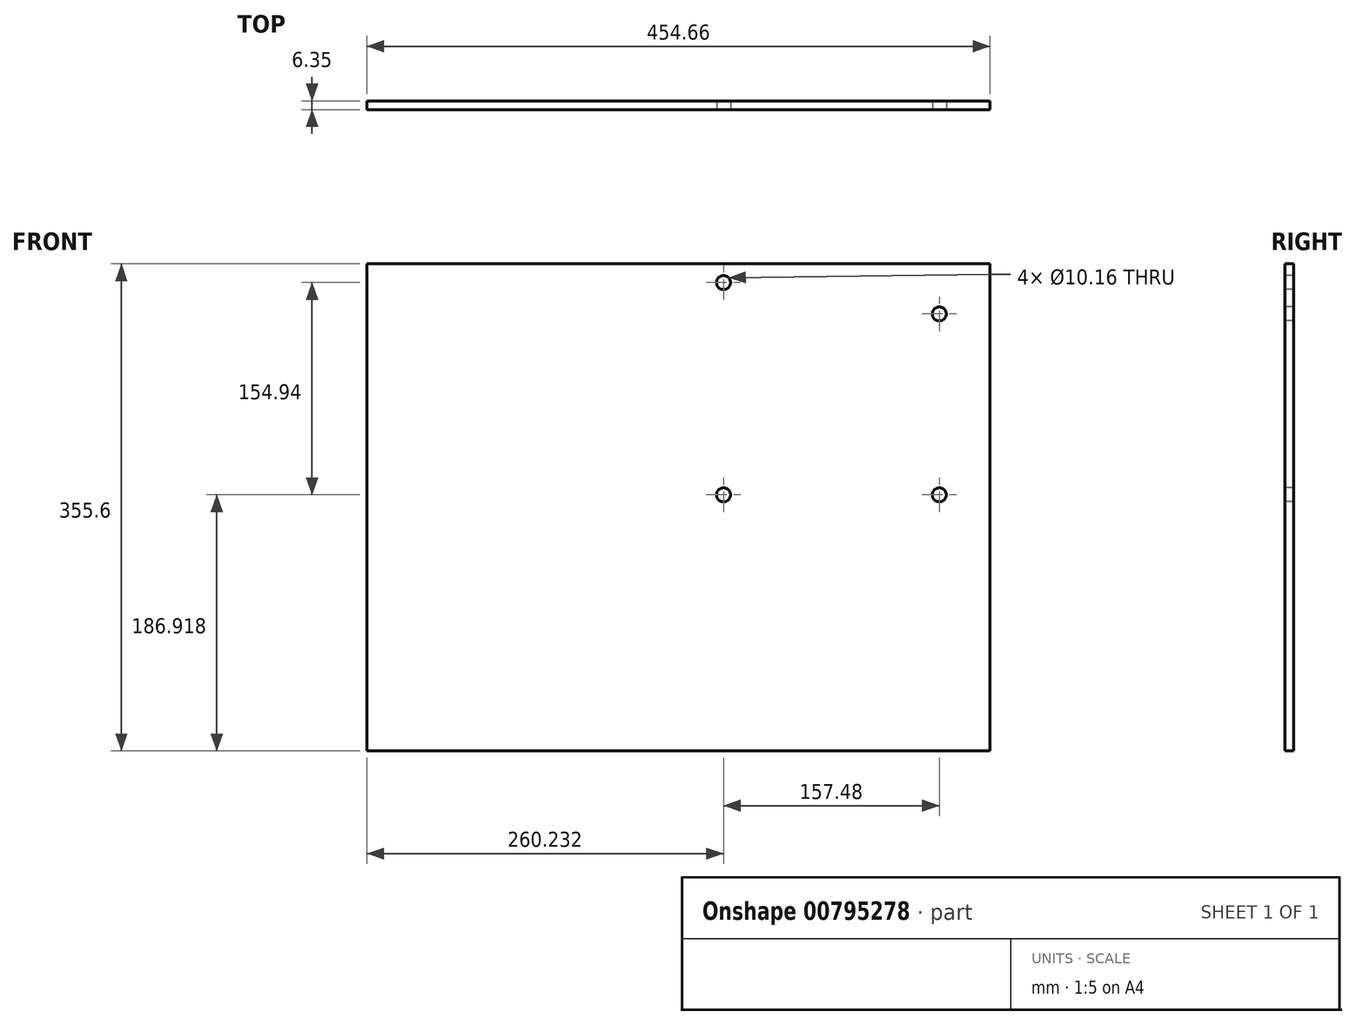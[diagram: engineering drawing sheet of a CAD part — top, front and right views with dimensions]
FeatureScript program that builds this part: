
annotation { "Feature Type Name" : "Feature", "Feature Type Description" : "" }
export const myFeature = defineFeature(function(context is Context, id is Id, definition is map)
    precondition{}
    {
        {
            var Q0;
            Q0=qCreatedBy(makeId("Front.planeOp"),FACE);
            var sketch = newSketch(context, id + "F0", { "sketchPlane" : qUnion([Q0])});
            skLineSegment(sketch, "E0.bottom", {"start": v(227.33, -177.8) * mm, "end": v(-227.33, -177.8) * mm});
            skLineSegment(sketch, "E0.top", {"start": v(227.33, 177.8) * mm, "end": v(-227.33, 177.8) * mm});
            skLineSegment(sketch, "E0.left", {"start": v(227.33, -177.8) * mm, "end": v(227.33, 177.8) * mm});
            skLineSegment(sketch, "E0.right", {"start": v(-227.33, -177.8) * mm, "end": v(-227.33, 177.8) * mm});
            skPoint(sketch, "E0.middle", {"position": v(0, 0) * mm});
            skSolve(sketch);
        }
        {
            var Q0;
            Q0=makeQuery(id+"F0.imprint","IMPRINT",FACE,{"disambiguationData":[TD([[makeQuery(id+"F0.imprint","IMPRINT",EDGE,{"derivedFrom":sQuery(id+"F0.wireOp",EDGE,"E0.bottom")}),-1.0]])]});
            extrude(context, id + "F1", {"entities" : qUnion([Q0]), "depth" : 6.35 * mm, "offsetDistance" : 25.4 * mm});
        }
        {
            var Q0;
            Q0=makeQuery(id+"F1.opExtrude","CAP_FACE",FACE,{"disambiguationData":[OSD([sQuery(id+"F0.wireOp",EDGE,"E0.bottom"),sQuery(id+"F0.wireOp",EDGE,"E0.top"),sQuery(id+"F0.wireOp",EDGE,"E0.left"),sQuery(id+"F0.wireOp",EDGE,"E0.right")])],"isStart":false});
            var sketch = newSketch(context, id + "F2", { "sketchPlane" : qUnion([Q0])});
            skCircle(sketch, "E1", {"center": v(178.6, 274.96) * mm, "radius": 3.81 * mm, "construction": true});
            skCircle(sketch, "E2", {"center": v(18.59, 274.96) * mm, "radius": 3.81 * mm, "construction": true});
            skLineSegment(sketch, "E3", {"start": v(18.59, 274.96) * mm, "end": v(178.6, 274.96) * mm, "construction": true});
            skCircle(sketch, "E4", {"center": v(-50, 274.96) * mm, "radius": 3.81 * mm, "construction": true});
            skLineSegment(sketch, "E5", {"start": v(-50, 274.96) * mm, "end": v(18.59, 274.96) * mm, "construction": true});
            skLineSegment(sketch, "E6", {"start": v(178.6, 274.96) * mm, "end": v(178.6, 408.3) * mm, "construction": true});
            skLineSegment(sketch, "E7", {"start": v(18.59, 274.96) * mm, "end": v(18.59, 436.93) * mm, "construction": true});
            skLineSegment(sketch, "E8", {"start": v(18.59, 436.93) * mm, "end": v(178.6, 408.3) * mm, "construction": true});
            skLineSegment(sketch, "E9", {"start": v(18.59, 436.93) * mm, "end": v(-29.04, 436.93) * mm, "construction": true});
            skCircle(sketch, "E10", {"center": v(-29.04, 436.93) * mm, "radius": 3.81 * mm, "construction": true});
            skCircle(sketch, "E11", {"center": v(18.59, 436.93) * mm, "radius": 3.81 * mm, "construction": true});
            skCircle(sketch, "E12", {"center": v(178.6, 408.3) * mm, "radius": 3.81 * mm, "construction": true});
            skCircle(sketch, "E13", {"center": v(32.9, 164.06) * mm, "radius": 5.08 * mm});
            skLineSegment(sketch, "E14", {"start": v(32.9, 164.06) * mm, "end": v(32.9, 9.12) * mm, "construction": true});
            skCircle(sketch, "E15", {"center": v(32.9, 9.12) * mm, "radius": 5.08 * mm});
            skLineSegment(sketch, "E16", {"start": v(32.9, 9.12) * mm, "end": v(190.38, 9.12) * mm, "construction": true});
            skCircle(sketch, "E17", {"center": v(190.38, 9.12) * mm, "radius": 5.08 * mm});
            skLineSegment(sketch, "E18", {"start": v(190.38, 164.06) * mm, "end": v(32.9, 164.06) * mm, "construction": true});
            skLineSegment(sketch, "E19", {"start": v(190.38, 164.06) * mm, "end": v(190.38, 141.2) * mm, "construction": true});
            skCircle(sketch, "E20", {"center": v(190.38, 141.2) * mm, "radius": 5.08 * mm});
            skSolve(sketch);
        }
        {
            var Q0;
            Q0=makeQuery(id+"F2.imprint","IMPRINT",FACE,{"disambiguationData":[TD([[makeQuery(id+"F2.imprint","IMPRINT",EDGE,{"derivedFrom":sQuery(id+"F2.wireOp",EDGE,"E13")}),1.0]])]});
            var Q1;
            Q1=makeQuery(id+"F2.imprint","IMPRINT",FACE,{"disambiguationData":[TD([[makeQuery(id+"F2.imprint","IMPRINT",EDGE,{"derivedFrom":sQuery(id+"F2.wireOp",EDGE,"E20")}),1.0]])]});
            var Q2;
            Q2=makeQuery(id+"F2.imprint","IMPRINT",FACE,{"disambiguationData":[TD([[makeQuery(id+"F2.imprint","IMPRINT",EDGE,{"derivedFrom":sQuery(id+"F2.wireOp",EDGE,"E17")}),1.0]])]});
            var Q3;
            Q3=makeQuery(id+"F2.imprint","IMPRINT",FACE,{"disambiguationData":[TD([[makeQuery(id+"F2.imprint","IMPRINT",EDGE,{"derivedFrom":sQuery(id+"F2.wireOp",EDGE,"E15")}),1.0]])]});
            extrude(context, id + "F3", {"entities" : qUnion([Q0, Q1, Q2, Q3]), "operationType" : NewBodyOperationType.REMOVE, "endBound" : BoundingType.UP_TO_NEXT, "oppositeDirection" : true, "depth" : 25.4 * mm, "offsetDistance" : 25.4 * mm});
        }
    });
